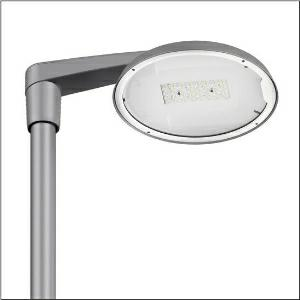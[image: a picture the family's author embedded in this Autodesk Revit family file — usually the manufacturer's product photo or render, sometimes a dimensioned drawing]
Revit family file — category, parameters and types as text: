
# Revit family: dl_r__50_iq_mini___st0_5a_5xa248b41f08ke_519f
name_source: partatom
category: Lighting Fixtures
units: mm (PartAtom-declared; Revit-internal decimal feet)

## family parameters
Cut with Voids When Loaded = No
Host = Face
Light Source = No
Part Type = Normal
Room Calculation Point = No
Round Connector Dimension = Use Diameter
Shared = No

## types (1)
- --- (1 x LED, 5510 lm, 30.8 W, 4000K)
    Apparent Load = 31 VA
    CIE Flux Codes = 43 76 97 100 100
    Color Rendering = 70
    Color Temperature = 4000K
    Default Elevation = 1800 mm
    Description = DL® 50 iQ mini, mast luminaire, primary light control with lens, of PMMA, primary optical cover: cover, of toughened safety glass, transparent, light distribution: ST0.5a, light emission: direct distribution, primary light characteristic: asymmetric, installation type: side-entry, post-top, LED, High Power LED, rated luminous flux: 5.510lm, luminous efficacy: 179lm/W, light colour: 740, colour temperature: 4000K, control gear: iQ Street-Remote, control: optimised constant luminous flux control (CLO 2.0), Desk-Remote (wireless, voltage-free reading and setting of iQ features in the workshop via application-optimized NFC function/RFID function), Light-Fading, Smart-Wire, Night-Set, Lumen-Switch, Temp-Guard, Auto-Match, Street-Remote, mains connection: 230..240V, AC, 50/60Hz, connection cable pre-assembled, cable length: 6,5m, start of lifetime: 31W, end of service life: 32W, reduction: 15W, luminaire housing, of diecast aluminium, powder-coated, Siteco® metallic grey (DB 702S), inclination adjustable: 0°, 5°, 10° (post-top) | 0°, -5°, -10°, -15° (side-entry), please order mast post-top element or mast side-entry element separately, diameter: 500mm, height: 115mm, post-top: for spigot size d x l = 76 x 100mm; with reducer (optional accessory) 60 x 100mm | side-entry: for spigot size d x l = 60 x 100mm; with reducer (optional accessory) 42 x 100mm, mounting height: 4..6m, protection rating (complete): IP66, insulation class (complete): insulation class II (safety insulation), certification: CE, ENEC, ENEC+, VDE, impact resistance: IK08, permissible operating ambient temperature for outdoor applications: -25..+40°C, standard-compliant lighting for roads and squares, packaging unit: 1 piece

Light Distribution: ST0.5a
    Height = 115 mm
    Lamp = 1 x LED
    Lamp Light Flux = 5510 lm
    Lamp Power = 30.8 W
    Lamp count = 1
    Length = 500 mm
    Luminous efficacy = 179 lm/W
    Manufacturer = Siteco
    ModVariant = No
    Model = 5XA248B41F08KE
    Number of Poles = 1
    OnlyDefault = Yes
    Power Factor = 1
    Product Name = DL® 50 iQ mini | ST0.5a
    Product group = mast luminaire | pylon top
    ProductGroupID = 6100
    Protection Class = Protection class II
    Protection Degree = IP 66
    RLX_Detail_Level = 1
    RLX_Emergency_Light_Flux = 0 lm
    RLX_Emergency_Type = 0
    RLX_Emergency_Type_DB = No
    RlxData = <blob elided: 126717 chars, md5=825f4d12>
    Socket = socket
    Standby Power = 0 W
    System Light Flux = 5510 lm
    System Power = 31 W
    Type Comments = factory setting: luminous flux: 100 % | dim-lin: 254 | 329 mA
    Type Image = l_1251794.jpg
    URL = http://relux.com
    VarID = @adj_142958
    Voltage = 0 V
    Weight = 0.00 kg
    Width = 0 mm  [stored 0 ft]

note: [stored X ft] marks values corroborated as IEEE doubles in the binary element streams (Revit-internal decimal feet)

## geometry (parser evidence)
native form markers: Blend x4, Sweep x11
no freeform markers — native parametric forms only
